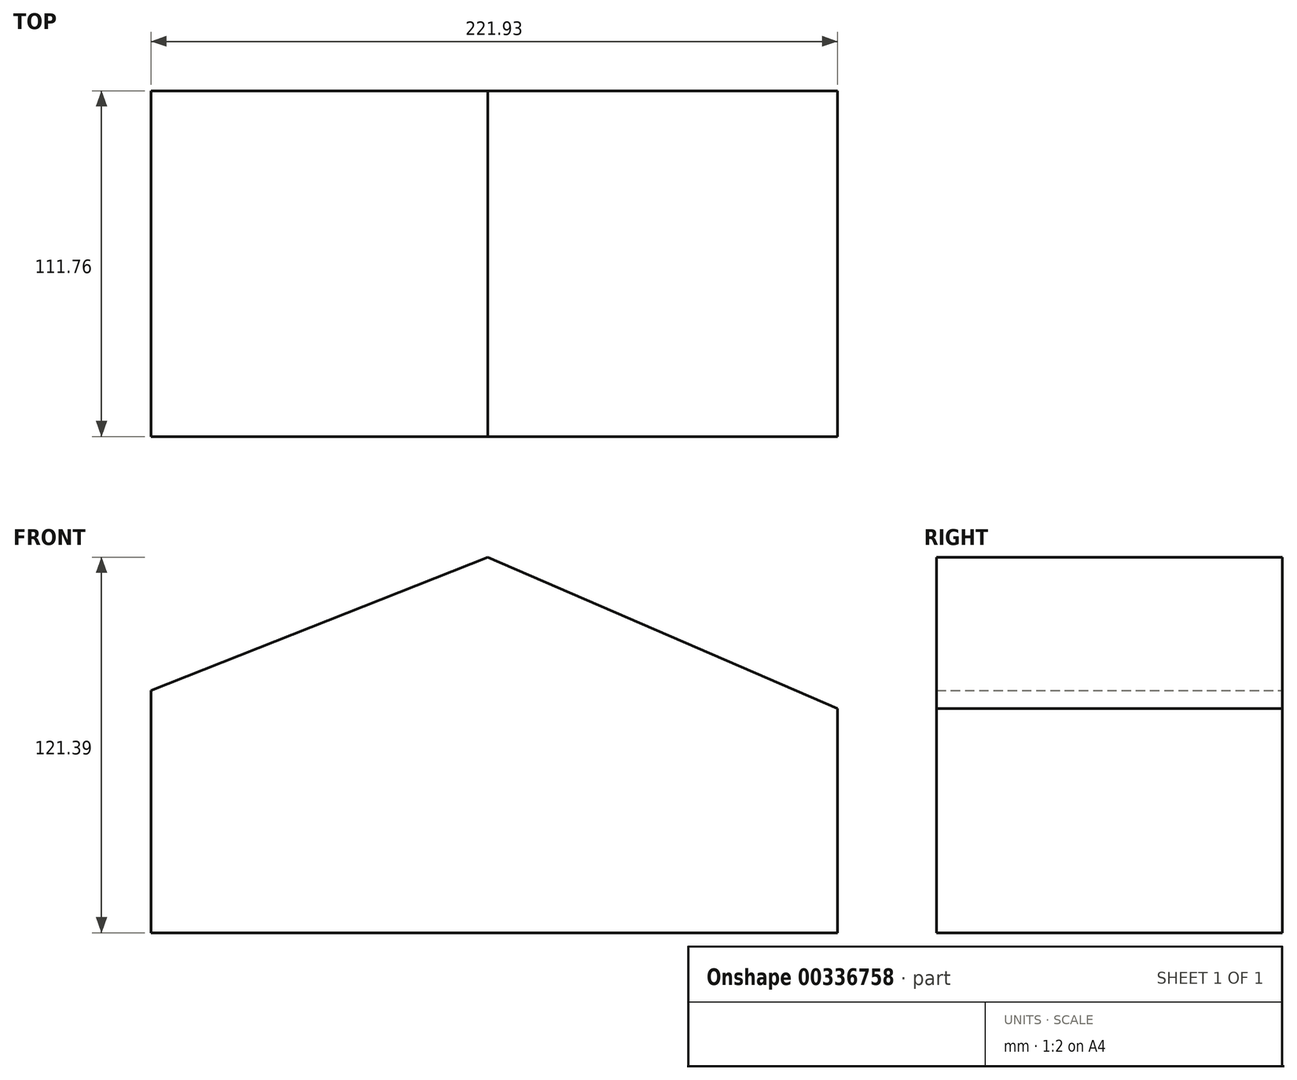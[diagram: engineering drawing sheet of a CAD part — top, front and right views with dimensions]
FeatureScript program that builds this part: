
annotation { "Feature Type Name" : "Feature", "Feature Type Description" : "" }
export const myFeature = defineFeature(function(context is Context, id is Id, definition is map)
    precondition{}
    {
        {
            var Q0;
            Q0=qCreatedBy(makeId("Front.planeOp"),FACE);
            var sketch = newSketch(context, id + "F0", { "sketchPlane" : qUnion([Q0])});
            skPoint(sketch, "E0.middle", {"position": v(0, 0) * mm});
            skLineSegment(sketch, "E1", {"start": v(-51.82, 24.23) * mm, "end": v(-108.85, 1.67) * mm});
            skLineSegment(sketch, "E2", {"start": v(-108.85, 1.67) * mm, "end": v(-51.82, -24.23) * mm});
            skLineSegment(sketch, "E3", {"start": v(51.82, 24.23) * mm, "end": v(113.08, 0) * mm});
            skLineSegment(sketch, "E4", {"start": v(113.08, 0) * mm, "end": v(51.82, -24.23) * mm});
            skLineSegment(sketch, "E5", {"start": v(0, -44.73) * mm, "end": v(51.82, -24.23) * mm});
            skLineSegment(sketch, "E6", {"start": v(-51.82, 24.23) * mm, "end": v(0, 44.73) * mm});
            skLineSegment(sketch, "E7", {"start": v(0, 44.73) * mm, "end": v(51.82, 24.23) * mm});
            skLineSegment(sketch, "E8", {"start": v(0, -44.73) * mm, "end": v(-51.82, -24.23) * mm});
            skLineSegment(sketch, "E9", {"start": v(-108.85, 1.67) * mm, "end": v(-108.85, -44.73) * mm});
            skLineSegment(sketch, "E10", {"start": v(-108.85, -44.73) * mm, "end": v(0, -44.73) * mm});
            skLineSegment(sketch, "E11", {"start": v(113.08, 0) * mm, "end": v(113.08, -44.73) * mm});
            skLineSegment(sketch, "E12", {"start": v(113.08, -44.73) * mm, "end": v(0, -44.73) * mm});
            skLineSegment(sketch, "E13", {"start": v(0, 44.73) * mm, "end": v(0, 76.66) * mm});
            skLineSegment(sketch, "E14", {"start": v(0, 76.66) * mm, "end": v(-108.85, 33.6) * mm});
            skLineSegment(sketch, "E15", {"start": v(-108.85, 33.6) * mm, "end": v(-108.85, 1.67) * mm});
            skLineSegment(sketch, "E16", {"start": v(0, 76.66) * mm, "end": v(113.08, 27.7) * mm});
            skLineSegment(sketch, "E17", {"start": v(113.08, 27.7) * mm, "end": v(113.08, 0) * mm});
            skSolve(sketch);
        }
        {
            var Q0;
            Q0 = qSketchRegion(id + "F0", true);
            extrude(context, id + "F1", {"entities" : qUnion([Q0]), "depth" : 111.76 * mm});
        }
    });
